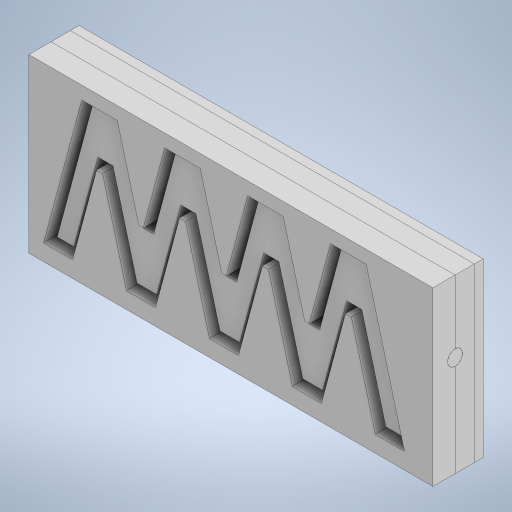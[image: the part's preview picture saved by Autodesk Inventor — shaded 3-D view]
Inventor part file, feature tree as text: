
AUTODESK INVENTOR PART (.ipt)
format: ipt  version: 2024 (Build 280153000, 153)  size: 590,336 bytes
history: native  units: mm
features: extrude x9, sketch x8, plane x4, split x4, boolean_combine x2, projected_geometry x2, other x2, pattern_linear x1, chamfer x1, shell x1
ambient origin geometry x8: Origin, YZ Plane, XZ Plane, XY Plane, X Axis, Y Axis, Z Axis, Center Point
bodies: Solid1 (feature_tree), Solid2 (feature_tree), Solid3 (feature_tree), Solid4 (feature_tree), Solid5 (feature_tree), Solid6 (feature_tree), Solid7 (feature_tree), Solid8 (feature_tree), Solid9 (feature_tree), Solid10 (feature_tree)
feature tree (34):
  extrude  "Extrusion1"  TaperAngle=75.0deg  [1 undecoded]
  pattern_linear  "Rectangular Pattern1"  Count1=5  [1 undecoded]
  chamfer  "Chamfer1"  Distance=15.0mm
  shell  "Shell1"  Thickness=40.0mm
  sketch  "Sketch2"  dims[d3=18.0mm]
  extrude  "Extrusion2"  Depth=2.0mm
  extrude  "Extrusion3"  Depth=2.0mm
  extrude  "Extrusion4"  Depth=3.0mm TaperAngle=0.0deg
  extrude  "Extrusion5"  Depth=10.0mm TaperAngle=0.0deg
  boolean_combine  "Combine1"
  extrude  "Extrusion6"  Depth=3.0mm TaperAngle=0.0deg
  plane  "Work Plane1"
  split  "Split1"
  split  "Split2"
  boolean_combine  "Combine2"
  plane  "Work Plane2"
  sketch  "Sketch9"  dims[d17=4.0mm d18=0.0mm d19=3.0mm d20=0.0mm]
  sketch  "Sketch10"  dims[d21=1.0mm d22=0.0mm d23=0.5mm d24=0.0mm d25=3.0mm d26=0.0mm d27=0.0mm d28=31.0mm d29=0.0mm d30=3.0mm d31=2.0mm d32=45.0deg d33=0.0mm d34=0.0mm d35=0.0mm d39=62.5mm d40=0.0mm d41=10.0mm d42=0.0mm]
  extrude  "Extrusion7"  TaperAngle=0.0deg  [1 undecoded]
  split  "Split3"
  plane  "Work Plane3"
  split  "Split4"
  plane  "Work Plane4"
  extrude  "Extrusion8"  Depth=10.0mm TaperAngle=0.0deg
  sketch  "Sketch1"  dims[d0=75.0deg d1=75.0deg d2=50.0mm]
  sketch  "Sketch3"  dims[d4=2.0mm]
  sketch  "Sketch4"  dims[d5=12.0mm d6=15.0mm d7=0.0mm d8=40.0mm d10=28.058819mm]
  sketch  "Sketch5"  dims[d12=28.058819mm d13=2.0mm]
  projected_geometry  "Projected Loop1"
  sketch  "Sketch7"  dims[d14=5.0mm d16=2.0mm]
  other  "Srf1"
  other  "Work Axis1"
  projected_geometry  "Projected Loop3"
  extrude  "ExtrusionSrf1"  Depth=3.0mm TaperAngle=45.0deg
note: 3 required parameter values undecoded (feature->parameter linkage not recoverable at this tier; creation-order binding heuristic only, values carry confidence <= 0.55)
